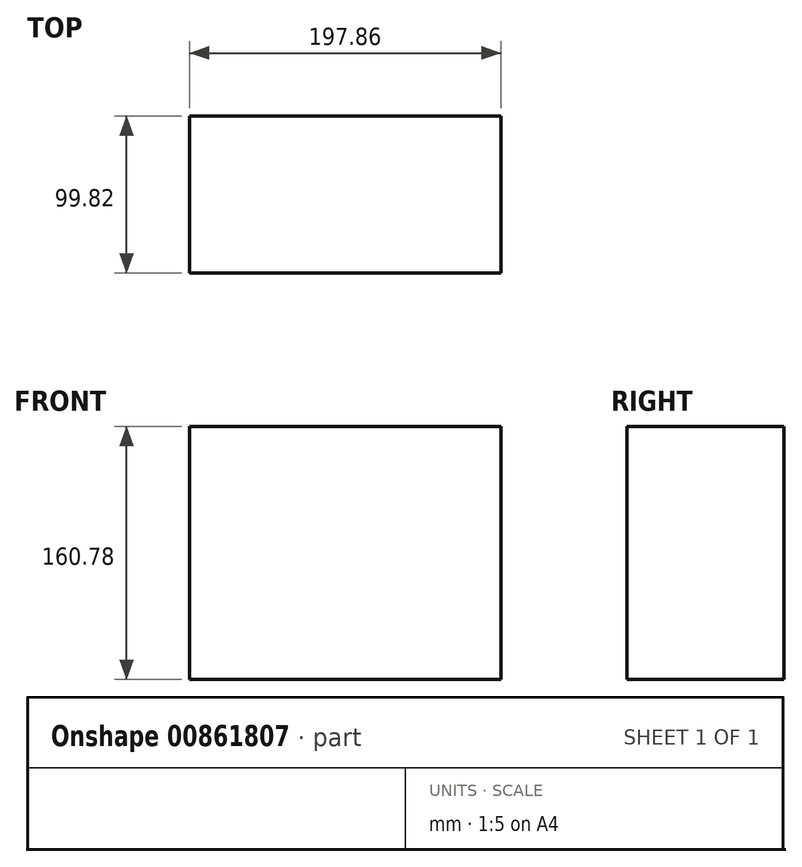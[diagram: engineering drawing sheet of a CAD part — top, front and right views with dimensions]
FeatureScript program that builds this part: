
annotation { "Feature Type Name" : "Feature", "Feature Type Description" : "" }
export const myFeature = defineFeature(function(context is Context, id is Id, definition is map)
    precondition{}
    {
        {
            var Q0;
            Q0=qCreatedBy(makeId("Front.planeOp"),FACE);
            var sketch = newSketch(context, id + "F0", { "sketchPlane" : qUnion([Q0])});
            skLineSegment(sketch, "E0.bottom", {"start": v(-265.56, -37.79) * mm, "end": v(-67.7, -37.79) * mm});
            skLineSegment(sketch, "E0.top", {"start": v(-265.56, -198.57) * mm, "end": v(-67.7, -198.57) * mm});
            skLineSegment(sketch, "E0.left", {"start": v(-265.56, -37.79) * mm, "end": v(-265.56, -198.57) * mm});
            skLineSegment(sketch, "E0.right", {"start": v(-67.7, -37.79) * mm, "end": v(-67.7, -198.57) * mm});
            skSolve(sketch);
        }
        {
            var Q0;
            Q0 = qSketchRegion(id + "F0", true);
            extrude(context, id + "F1", {"entities" : qUnion([Q0]), "flatOperationType" : FlatOperationType.REMOVE, "depth" : 99.82 * mm, "offsetDistance" : 25.4 * mm, "domain" : OperationDomain.MODEL});
        }
    });
